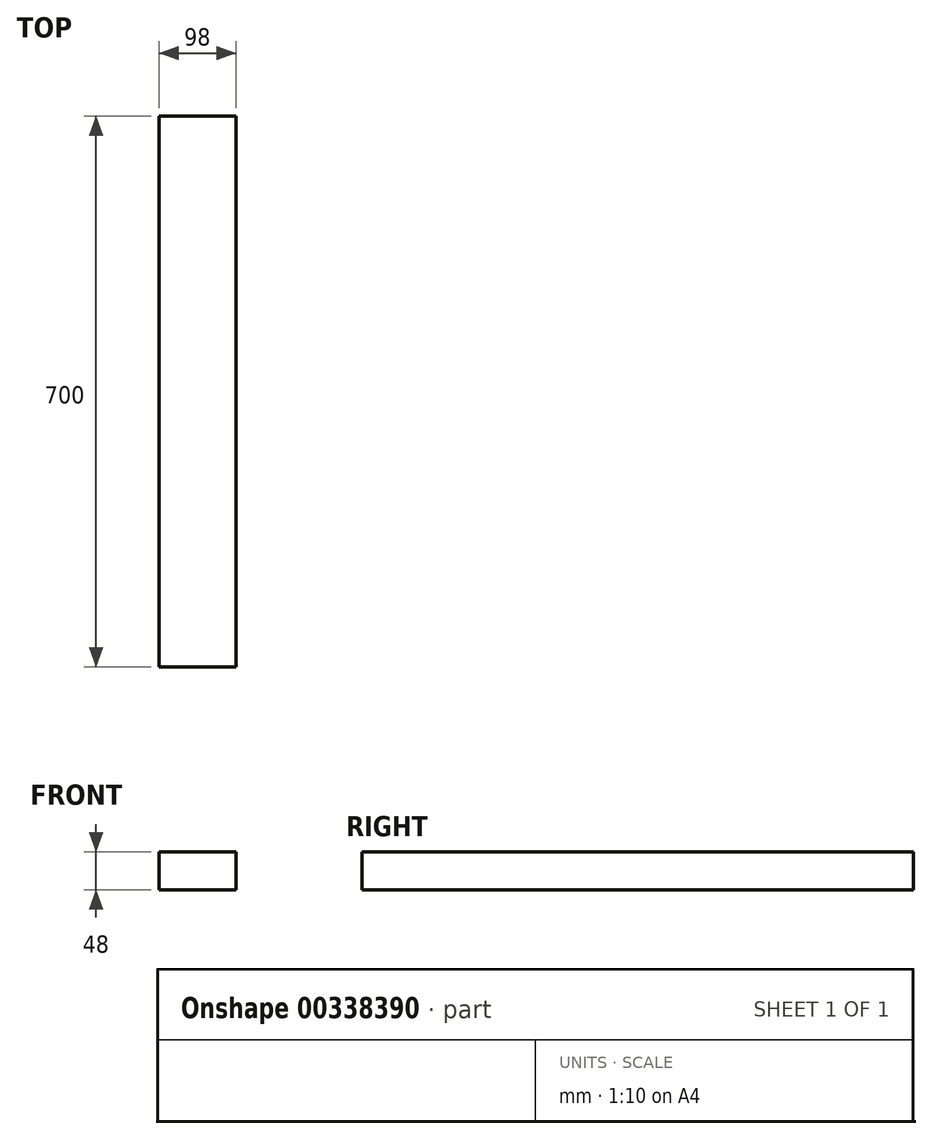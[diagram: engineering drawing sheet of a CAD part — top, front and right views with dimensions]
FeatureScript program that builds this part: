
annotation { "Feature Type Name" : "Feature", "Feature Type Description" : "" }
export const myFeature = defineFeature(function(context is Context, id is Id, definition is map)
    precondition{}
    {
        {
            var Q0;
            Q0=qCreatedBy(makeId("Front.planeOp"),FACE);
            var sketch = newSketch(context, id + "F0", { "sketchPlane" : qUnion([Q0])});
            skLineSegment(sketch, "E0.bottom", {"start": v(-49, -24) * mm, "end": v(49, -24) * mm});
            skLineSegment(sketch, "E0.top", {"start": v(-49, 24) * mm, "end": v(49, 24) * mm});
            skLineSegment(sketch, "E0.left", {"start": v(-49, -24) * mm, "end": v(-49, 24) * mm});
            skLineSegment(sketch, "E0.right", {"start": v(49, -24) * mm, "end": v(49, 24) * mm});
            skPoint(sketch, "E0.middle", {"position": v(0, 0) * mm});
            skSolve(sketch);
        }
        {
            var Q0;
            Q0=makeQuery(id+"F0.imprint","IMPRINT",FACE,{"disambiguationData":[TD([[makeQuery(id+"F0.imprint","IMPRINT",EDGE,{"derivedFrom":sQuery(id+"F0.wireOp",EDGE,"E0.bottom")}),1.0]])]});
            extrude(context, id + "F1", {"entities" : qUnion([Q0]), "depth" : 700 * mm});
        }
    });
